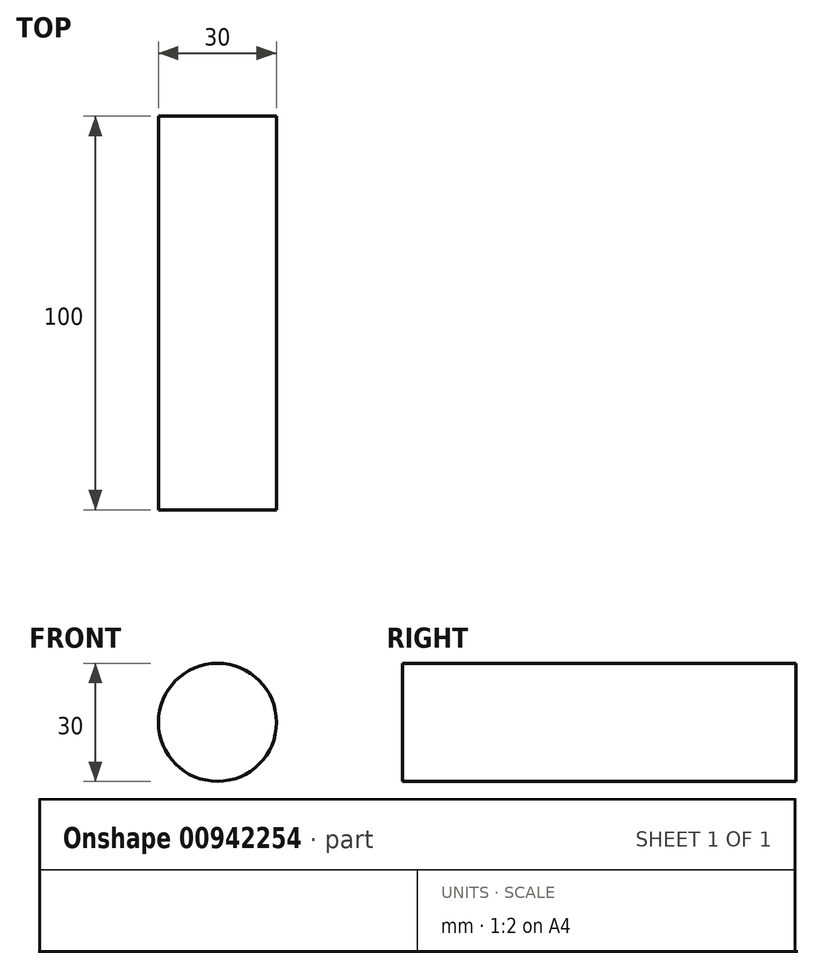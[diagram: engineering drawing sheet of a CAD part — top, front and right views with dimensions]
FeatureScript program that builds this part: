
annotation { "Feature Type Name" : "Feature", "Feature Type Description" : "" }
export const myFeature = defineFeature(function(context is Context, id is Id, definition is map)
    precondition{}
    {
        {
            var Q0;
            Q0=qCreatedBy(makeId("Front.planeOp"),FACE);
            var sketch = newSketch(context, id + "F0", { "sketchPlane" : qUnion([Q0])});
            skCircle(sketch, "E0", {"center": v(0, 0) * mm, "radius": 15 * mm});
            skSolve(sketch);
        }
        {
            var Q0;
            Q0=makeQuery(id+"F0.imprint","IMPRINT",FACE,{"disambiguationData":[TD([[makeQuery(id+"F0.imprint","IMPRINT",EDGE,{"derivedFrom":sQuery(id+"F0.wireOp",EDGE,"E0")}),1.0]])]});
            extrude(context, id + "F1", {"entities" : qUnion([Q0]), "oppositeDirection" : true, "depth" : 100 * mm, "offsetDistance" : 25 * mm});
        }
    });
